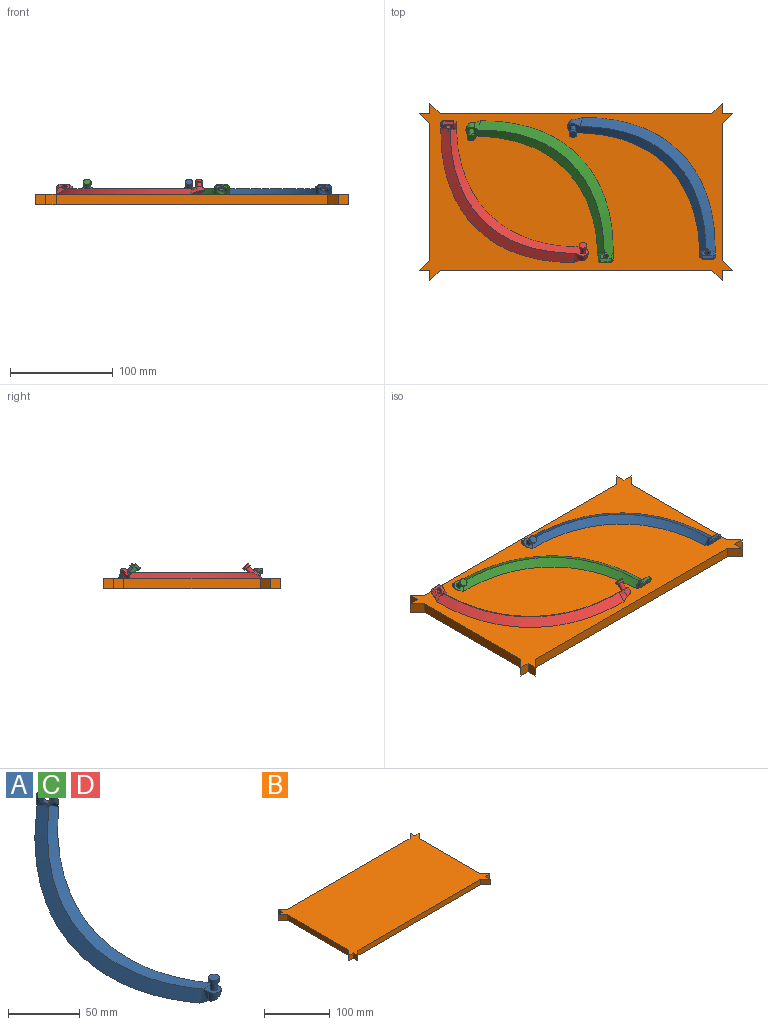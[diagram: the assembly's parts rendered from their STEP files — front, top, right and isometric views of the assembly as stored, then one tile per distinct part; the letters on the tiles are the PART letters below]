
ASSEMBLY  parts=4 mates=3
PART A: 41 faces, bbox 52.2x175.5x102 mm
  f0: plane 5.18x4.18mm, normal (0.79,0.61,-0.05), area 6mm2, adj f9,f23,f27
  f1: plane 5.11x4.38mm, normal (0.79,0.61,-0.05), area 6mm2, adj f9,f23,f33
  f2: plane 8.42x6.23mm, normal (-0.82,-0.41,-0.4), area 27.8mm2, adj f5,f19,f25,f33,f39,f40
  f3: plane 5.85x5.64mm, normal (-0.52,-0.76,-0.39), area 17.3mm2, adj f6,f18,f25,f27,f28,f31
  f4: cylinder r=180mm len=150.82mm, axis (1,0,0), area 1766.2mm2, adj f5,f6,f9,f11,f25,f26,f27
  f5: bspline ~160.22x93.24mm, area 2224.1mm2, adj f2,f4,f9,f13,f25,f26,f33
  f6: plane 5.86x3.44mm, normal (-0.58,-0.46,-0.67), area 0.1mm2, adj f3,f4,f25,f27
  f7: cylinder r=2.5mm len=6.12mm, axis (0.79,0.61,-0.05), area 55.5mm2, adj f23,f25
  f8: plane 3.12x1.11mm, normal (0.79,0.61,-0.05), area 1mm2, adj f23,f27,f30
  f9: plane 159.97x89.78mm, normal (0.54,0.41,-0.74), area 3428.4mm2, adj f0,f1,f4,f5,f10,f27,f33
  f10: plane 15.29x11.53mm, normal (0.59,0,-0.81), area 122mm2, adj f9,f11,f12,f13
  f11: plane 10x10mm, normal (0,0,1), area 69.6mm2, adj f4,f10,f12,f13,f14
  f12: cylinder r=5mm len=10mm, axis (0,0,1), area 57.1mm2, adj f10,f11,f13
  f13: bspline ~10x5mm, area 47.1mm2, adj f5,f10,f11,f12
  f14: cylinder r=2.5mm len=7.5mm, axis (0,0,-1), area 117.8mm2, adj f11,f15
  f15: plane 7.5x7.5mm, normal (0,0,-1), area 24.5mm2, adj f14,f16
  f16: cylinder r=3.75mm len=7.5mm, axis (0,0,-1), area 58.9mm2, adj f15,f17
  f17: plane 7.5x7.5mm, normal (0,0,1), area 44.2mm2, adj f16
  f18: plane 4.03x0.75mm, normal (0.62,-0.79,0.02), area 2.4mm2, adj f3,f21,f27,f28
  f19: plane 4.03x0.75mm, normal (-0.61,0.79,-0.01), area 2.4mm2, adj f2,f22,f33,f40
  f20: plane 3.13x0.99mm, normal (0.79,0.61,-0.05), area 1mm2, adj f23,f30,f33
  f21: plane 6.24x0.86mm, normal (0.61,-0.79,0.01), area 5.2mm2, adj f18,f27,f31,f32
  f22: plane 6.25x0.87mm, normal (-0.61,0.79,-0.01), area 5.2mm2, adj f19,f33,f37,f39
  f23: sphere r=7.5mm, area 73mm2, adj f0,f1,f7,f8,f20,f27,f30,f33
  f24: plane 8.91x7.23mm, normal (0.03,0.04,1), area 9.6mm2, adj f30,f32,f36,f37
  f25: plane 8.54x8.17mm, normal (-0.79,-0.61,0.05), area 42mm2, adj f2,f3,f4,f5,f6,f7,f26,f31
  f26: cylinder r=5mm len=3.7mm, axis (0.79,0.61,-0.05), area 3.1mm2, adj f4,f5,f25
  f27: plane 10.61x3.53mm, normal (0.99,-0.12,-0.02), area 29.4mm2, adj f0,f3,f4,f6,f8,f9,f18,f21
  f28: plane 2.28x2.27mm, normal (-0.12,-0.99,0.05), area 2.5mm2, adj f3,f18,f31
  f29: plane 3.09x2.3mm, normal (0.83,-0.08,0.56), area 4.2mm2, adj f27,f30,f32
  f30: plane 9.62x8.19mm, normal (0.58,0.46,0.67), area 24.8mm2, adj f8,f20,f23,f24,f29,f35
  f31: plane 5.38x3.22mm, normal (-0.12,-0.99,0.04), area 16.2mm2, adj f3,f21,f25,f28,f34
  f32: plane 2.38x2.21mm, normal (0.45,-0.53,0.72), area 2.8mm2, adj f21,f24,f29,f34
  f33: plane 10.63x3.45mm, normal (0.12,0.99,-0.04), area 29.3mm2, adj f1,f2,f5,f9,f19,f20,f22,f23
  f34: plane 3.09x2.17mm, normal (-0.08,-0.79,0.61), area 4.2mm2, adj f31,f32,f36
  f35: plane 3.09x2.3mm, normal (0.12,0.83,0.54), area 4.2mm2, adj f30,f33,f37
  f36: plane 9.8x8.31mm, normal (-0.54,-0.41,0.74), area 33mm2, adj f24,f25,f34,f38
  f37: plane 2.27x2.2mm, normal (-0.41,0.59,0.7), area 2.8mm2, adj f22,f24,f35,f38
  f38: plane 3.09x2.23mm, normal (-0.79,0.12,0.6), area 4.2mm2, adj f36,f37,f39
  f39: plane 5.44x3.26mm, normal (-0.99,0.12,0.02), area 15.8mm2, adj f2,f22,f25,f38,f40
  f40: plane 2.31x1.98mm, normal (-0.99,0.13,0.03), area 2.2mm2, adj f2,f19,f39
PART B: 22 faces, bbox 304.5x172.4x10 mm
  f0: plane 10x10mm, normal (0,-1,0), area 100mm2, adj f1,f19,f20,f21
  f1: plane 10x10mm, normal (-1,0,0), area 100mm2, adj f0,f2,f20,f21
  f2: plane 10x10mm, normal (0.71,-0.71,0), area 141.4mm2, adj f1,f3,f20,f21
  f3: plane 264.48x10mm, normal (0,-1,0), area 2644.8mm2, adj f2,f4,f20,f21
  f4: plane 10x10mm, normal (-0.71,-0.71,0), area 141.4mm2, adj f3,f5,f20,f21
  f5: plane 10x10mm, normal (1,0,0), area 100mm2, adj f4,f6,f20,f21
  f6: plane 10x10mm, normal (0,-1,0), area 100mm2, adj f5,f7,f20,f21
  f7: plane 10x10mm, normal (0.71,0.71,0), area 141.4mm2, adj f6,f8,f20,f21
  f8: plane 132.4x10mm, normal (1,0,0), area 1324mm2, adj f7,f9,f20,f21
  f9: plane 10x10mm, normal (0.71,-0.71,0), area 141.4mm2, adj f8,f10,f20,f21
  f10: plane 10x10mm, normal (0,1,0), area 100mm2, adj f9,f11,f20,f21
  f11: plane 10x10mm, normal (1,0,0), area 100mm2, adj f10,f12,f20,f21
  f12: plane 10x10mm, normal (-0.71,0.71,0), area 141.4mm2, adj f11,f13,f20,f21
  f13: plane 264.48x10mm, normal (0,1,0), area 2644.8mm2, adj f12,f14,f20,f21
  f14: plane 10x10mm, normal (0.71,0.71,0), area 141.4mm2, adj f13,f15,f20,f21
  f15: plane 10x10mm, normal (-1,0,0), area 100mm2, adj f14,f16,f20,f21
  f16: plane 10x10mm, normal (0,1,0), area 100mm2, adj f15,f17,f20,f21
  f17: plane 10x10mm, normal (-0.71,-0.71,0), area 141.4mm2, adj f16,f18,f20,f21
  f18: plane 132.4x10mm, normal (-1,0,0), area 1324mm2, adj f17,f19,f20,f21
  f19: plane 10x10mm, normal (-0.71,0.71,0), area 141.4mm2, adj f0,f18,f20,f21
  f20: plane 304.48x172.4mm, normal (0,0,1), area 43754.8mm2, adj f0,f1,f2,f3,f4,f5,f6,f7
  f21: plane 304.48x172.4mm, normal (0,0,-1), area 43754.8mm2, adj f0,f1,f2,f3,f4,f5,f6,f7
PART C: same geometry as A
PART D: same geometry as A
PLACE A rot(axis=(0.18,0.36,-0.92),130.3deg) t=(-4.09,1.91,76.97)mm
PLACE B t=(-1.74,-0.18,-166.69)mm fixed
PLACE C rot(axis=(0.18,0.36,-0.92),130.3deg) t=(-103.16,-1.37,76.97)mm
PLACE D rot(axis=(-0.58,0.29,0.76),67.3deg) t=(4.48,1.68,76.97)mm
MATE planar A.f9 <-> B.f20  axis (0,0,-1) through (82.99,22.51,5.71)mm
MATE planar D.f9 <-> B.f20  axis (0,0,-1) through (-82.59,-18.92,5.71)mm
MATE planar C.f9 <-> B.f20  axis (0,0,-1) through (-16.08,19.23,5.71)mm
